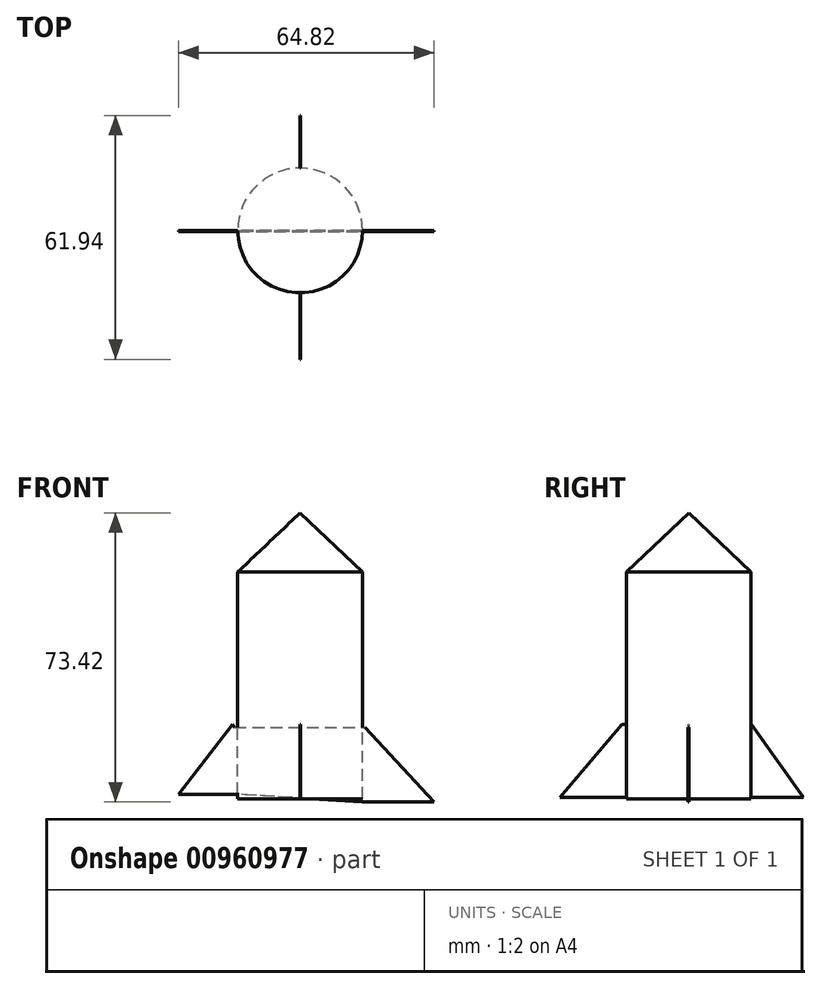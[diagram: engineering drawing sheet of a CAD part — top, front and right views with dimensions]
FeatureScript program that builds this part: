
annotation { "Feature Type Name" : "Feature", "Feature Type Description" : "" }
export const myFeature = defineFeature(function(context is Context, id is Id, definition is map)
    precondition{}
    {
        {
            var Q0;
            Q0=qCreatedBy(makeId("Front.planeOp"),FACE);
            var sketch = newSketch(context, id + "F0", { "sketchPlane" : qUnion([Q0])});
            skLineSegment(sketch, "E0", {"start": v(-15.85, 36.93) * mm, "end": v(-15.85, -20.68) * mm});
            skLineSegment(sketch, "E1", {"start": v(-15.85, -20.68) * mm, "end": v(0, -20.68) * mm});
            skLineSegment(sketch, "E2", {"start": v(-15.85, 36.93) * mm, "end": v(0, 36.93) * mm});
            skLineSegment(sketch, "E3", {"start": v(0, 36.93) * mm, "end": v(0, -20.68) * mm});
            skSolve(sketch);
        }
        {
            var Q0;
            Q0=makeQuery(id+"F0.imprint","IMPRINT",FACE,{"disambiguationData":[TD([[makeQuery(id+"F0.imprint","IMPRINT",EDGE,{"derivedFrom":sQuery(id+"F0.wireOp",EDGE,"E0")}),1.0]])]});
            var Q1;
            Q1=sQuery(id+"F0.wireOp",EDGE,"E3");
            revolve(context, id + "F1", {"surfaceOperationType" : NewSurfaceOperationType.NEW, "entities" : qUnion([Q0]), "axis" : qUnion([Q1]), "revolveType" : RevolveType.FULL});
        }
        {
            var Q0;
            Q0=qCreatedBy(makeId("Front.planeOp"),FACE);
            var sketch = newSketch(context, id + "F2", { "sketchPlane" : qUnion([Q0])});
            skLineSegment(sketch, "E4", {"start": v(-17.16, -1.8) * mm, "end": v(-30.85, -19.56) * mm});
            skLineSegment(sketch, "E5", {"start": v(-30.85, -19.56) * mm, "end": v(-15.48, -19.56) * mm});
            skLineSegment(sketch, "E6", {"start": v(-15.48, -19.56) * mm, "end": v(-15.48, -1.8) * mm});
            skLineSegment(sketch, "E7", {"start": v(-16.68, -2.52) * mm, "end": v(16.44, -2.52) * mm});
            skLineSegment(sketch, "E8", {"start": v(16.44, -2.52) * mm, "end": v(33.97, -21.48) * mm});
            skLineSegment(sketch, "E9", {"start": v(33.97, -21.48) * mm, "end": v(15.72, -21.48) * mm});
            skLineSegment(sketch, "E10", {"start": v(-17.16, -1.8) * mm, "end": v(-16.68, -2.52) * mm});
            skLineSegment(sketch, "E11", {"start": v(15.72, -21.48) * mm, "end": v(-15.48, -19.56) * mm});
            skSolve(sketch);
        }
        {
            var Q0;
            Q0=qCreatedBy(makeId("Right.planeOp"),FACE);
            var sketch = newSketch(context, id + "F3", { "sketchPlane" : qUnion([Q0])});
            skLineSegment(sketch, "E12", {"start": v(15.72, -20.28) * mm, "end": v(29.17, -20.28) * mm});
            skLineSegment(sketch, "E13", {"start": v(29.17, -20.28) * mm, "end": v(15.96, -1.8) * mm});
            skLineSegment(sketch, "E14", {"start": v(15.96, -1.8) * mm, "end": v(-16.92, -1.8) * mm});
            skLineSegment(sketch, "E15", {"start": v(-16.92, -1.8) * mm, "end": v(-32.77, -20.28) * mm});
            skLineSegment(sketch, "E16", {"start": v(-32.77, -20.28) * mm, "end": v(-16.92, -20.28) * mm});
            skLineSegment(sketch, "E17", {"start": v(-16.92, -20.28) * mm, "end": v(-16.92, -1.8) * mm});
            skLineSegment(sketch, "E18", {"start": v(-16.92, -20.28) * mm, "end": v(15.72, -20.28) * mm});
            skSolve(sketch);
        }
        {
            var Q0;
            Q0=makeQuery(id+"F3.imprint","IMPRINT",FACE,{"disambiguationData":[TD([[makeQuery(id+"F3.imprint","IMPRINT",EDGE,{"derivedFrom":sQuery(id+"F3.wireOp",EDGE,"E12")}),1.0]])]});
            var Q1;
            Q1=makeQuery(id+"F3.imprint","IMPRINT",FACE,{"disambiguationData":[TD([[makeQuery(id+"F3.imprint","IMPRINT",EDGE,{"derivedFrom":sQuery(id+"F3.wireOp",EDGE,"E15")}),1.0]])]});
            extrude(context, id + "F4", {"entities" : qUnion([Q0, Q1]), "operationType" : NewBodyOperationType.ADD, "depth" : 0.1 * mm, "offsetDistance" : 25.4 * mm});
        }
        {
            var Q0;
            Q0 = qSketchRegion(id + "F2", true);
            extrude(context, id + "F5", {"entities" : qUnion([Q0]), "depth" : 0.25 * mm, "offsetDistance" : 25.4 * mm});
        }
        {
            var Q0;
            Q0=qCreatedBy(makeId("Right.planeOp"),FACE);
            var sketch = newSketch(context, id + "F6", { "sketchPlane" : qUnion([Q0])});
            skLineSegment(sketch, "E19", {"start": v(15.85, 36.92) * mm, "end": v(0, 51.94) * mm});
            skLineSegment(sketch, "E20", {"start": v(0, 51.94) * mm, "end": v(0, 36.92) * mm});
            skLineSegment(sketch, "E21", {"start": v(0, 36.92) * mm, "end": v(15.85, 36.92) * mm});
            skSolve(sketch);
        }
        {
            var Q0;
            Q0 = qSketchRegion(id + "F6", true);
            var Q1;
            Q1=sQuery(id+"F6.wireOp",EDGE,"E20");
            revolve(context, id + "F7", {"operationType" : NewBodyOperationType.ADD, "surfaceOperationType" : NewSurfaceOperationType.NEW, "entities" : qUnion([Q0]), "axis" : qUnion([Q1]), "revolveType" : RevolveType.FULL});
        }
    });
